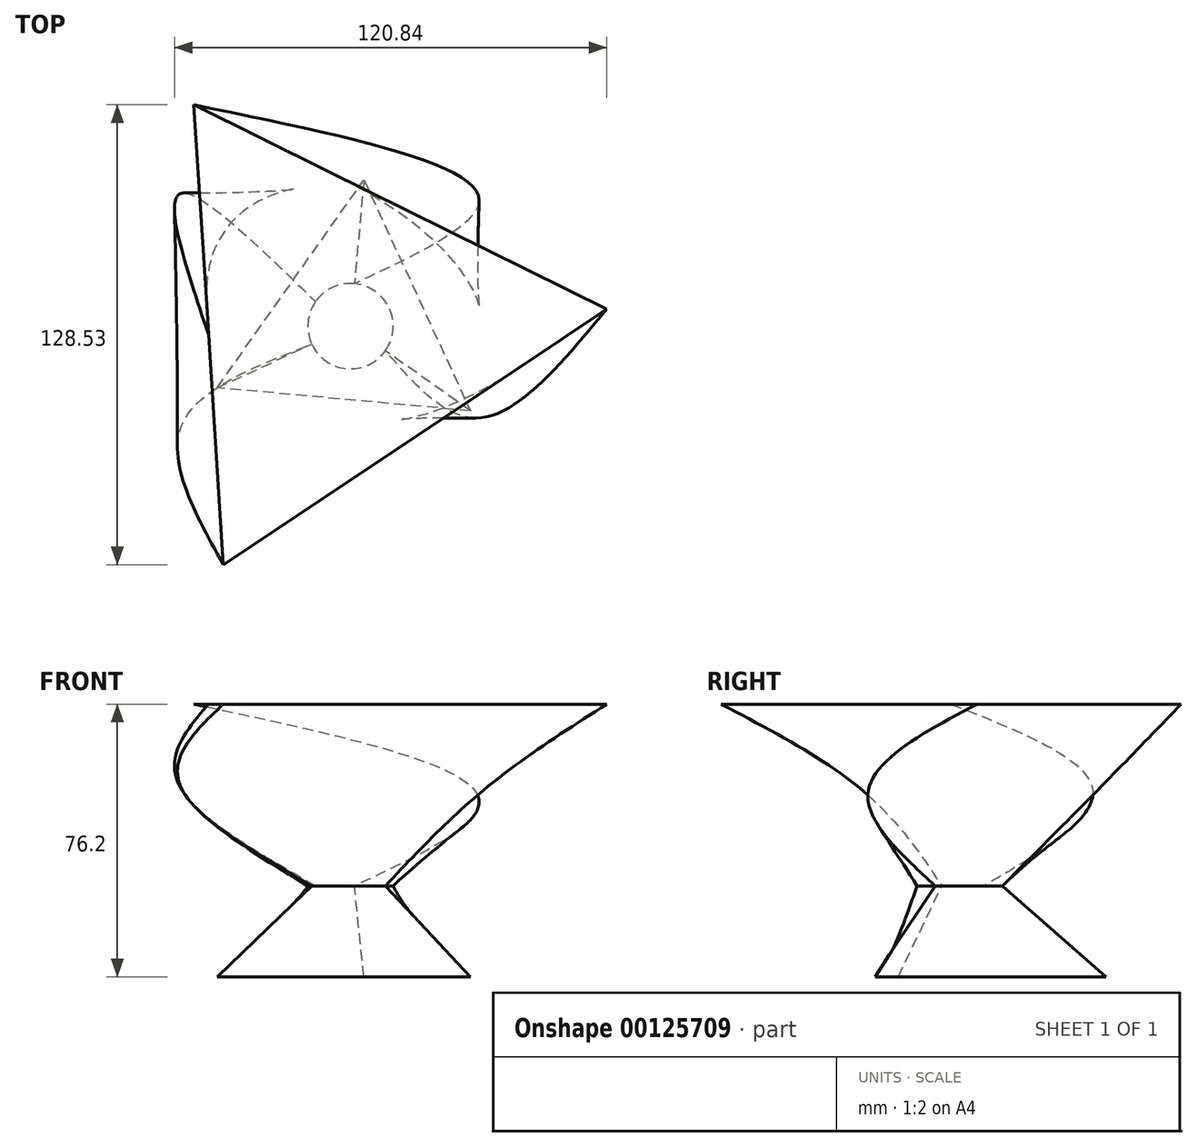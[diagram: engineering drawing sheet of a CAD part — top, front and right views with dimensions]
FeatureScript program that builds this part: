
annotation { "Feature Type Name" : "Feature", "Feature Type Description" : "" }
export const myFeature = defineFeature(function(context is Context, id is Id, definition is map)
    precondition{}
    {
        {
            var Q0;
            Q0=qCreatedBy(makeId("Top.planeOp"),FACE);
            cPlane(context, id + "F0", {"entities" : qUnion([Q0]), "cplaneType" : CPlaneType.OFFSET, "offset" : 25.4 * mm, "width" : 152.4 * mm, "height" : 152.4 * mm});
        }
        {
            var Q0;
            Q0=qCreatedBy(id+"F0.planeOp",FACE);
            cPlane(context, id + "F1", {"entities" : qUnion([Q0]), "cplaneType" : CPlaneType.OFFSET, "offset" : 25.4 * mm, "width" : 152.4 * mm, "height" : 152.4 * mm});
        }
        {
            var Q0;
            Q0=qCreatedBy(id+"F1.planeOp",FACE);
            cPlane(context, id + "F2", {"entities" : qUnion([Q0]), "cplaneType" : CPlaneType.OFFSET, "offset" : 25.4 * mm, "width" : 152.4 * mm, "height" : 152.4 * mm});
        }
        {
            var Q0;
            Q0=qCreatedBy(id+"F0.planeOp",FACE);
            var sketch = newSketch(context, id + "F3", { "sketchPlane" : qUnion([Q0])});
            skCircle(sketch, "E0", {"center": v(0, 0) * mm, "radius": 11.93 * mm});
            skSolve(sketch);
        }
        {
            var Q0;
            Q0=qCreatedBy(makeId("Top.planeOp"),FACE);
            var sketch = newSketch(context, id + "F4", { "sketchPlane" : qUnion([Q0])});
            skCircle(sketch, "E1.cCircle", {"center": v(0, 0) * mm, "radius": 20.52 * mm, "construction": true});
            skLineSegment(sketch, "E1.0", {"start": v(3.74, 40.88) * mm, "end": v(33.53, -23.68) * mm});
            skLineSegment(sketch, "E1.1", {"start": v(33.53, -23.68) * mm, "end": v(-37.27, -17.2) * mm});
            skLineSegment(sketch, "E1.2", {"start": v(-37.27, -17.2) * mm, "end": v(3.74, 40.88) * mm});
            skPoint(sketch, "E1.0.midPoint", {"position": v(18.64, 8.6) * mm});
            skSolve(sketch);
        }
        {
            var Q0;
            Q0=makeQuery(id+"F4.imprint","IMPRINT",FACE,{"disambiguationData":[TD([[makeQuery(id+"F4.imprint","IMPRINT",EDGE,{"derivedFrom":sQuery(id+"F4.wireOp",EDGE,"E1.0")}),-1.0]])]});
            var Q1;
            Q1=makeQuery(id+"F3.imprint","IMPRINT",FACE,{"disambiguationData":[TD([[makeQuery(id+"F3.imprint","IMPRINT",EDGE,{"derivedFrom":sQuery(id+"F3.wireOp",EDGE,"E0")}),1.0]])]});
            loft(context, id + "F5", {"sheetProfilesArray" : [{ "sheetProfileEntities" : qUnion([Q0]) }, { "sheetProfileEntities" : qUnion([Q1]) }]});
        }
        {
            var Q0;
            Q0=qCreatedBy(id+"F1.planeOp",FACE);
            var sketch = newSketch(context, id + "F6", { "sketchPlane" : qUnion([Q0])});
            skLineSegment(sketch, "E2.bottom", {"start": v(35.54, -25.67) * mm, "end": v(-46.17, -25.67) * mm});
            skLineSegment(sketch, "E2.top", {"start": v(35.54, 37.2) * mm, "end": v(-46.17, 37.2) * mm});
            skLineSegment(sketch, "E2.left", {"start": v(35.54, -25.67) * mm, "end": v(35.54, 37.2) * mm});
            skLineSegment(sketch, "E2.right", {"start": v(-46.17, -25.67) * mm, "end": v(-46.17, 37.2) * mm});
            skSolve(sketch);
        }
        {
            var Q0;
            Q0=qCreatedBy(id+"F2.planeOp",FACE);
            var sketch = newSketch(context, id + "F7", { "sketchPlane" : qUnion([Q0])});
            skCircle(sketch, "E3.cCircle", {"center": v(-2.58, 0) * mm, "radius": 37.18 * mm, "construction": true});
            skLineSegment(sketch, "E3.0", {"start": v(71.63, 4.79) * mm, "end": v(-35.54, -66.66) * mm});
            skLineSegment(sketch, "E3.1", {"start": v(-35.54, -66.66) * mm, "end": v(-43.83, 61.87) * mm});
            skLineSegment(sketch, "E3.2", {"start": v(-43.83, 61.87) * mm, "end": v(71.63, 4.79) * mm});
            skPoint(sketch, "E3.0.midPoint", {"position": v(18.05, -30.94) * mm});
            skSolve(sketch);
        }
        {
            var Q1;
            Q1=makeQuery(id+"F7.imprint","IMPRINT",FACE,{"disambiguationData":[TD([[makeQuery(id+"F7.imprint","IMPRINT",EDGE,{"derivedFrom":sQuery(id+"F7.wireOp",EDGE,"E3.0")}),-1.0]])]});
            var Q2;
            Q2=makeQuery(id+"F6.imprint","IMPRINT",FACE,{"disambiguationData":[TD([[makeQuery(id+"F6.imprint","IMPRINT",EDGE,{"derivedFrom":sQuery(id+"F6.wireOp",EDGE,"E2.bottom")}),-1.0]])]});
            var Q3;
            Q3=makeQuery(id+"F5.opLoft","CAP_FACE",FACE,{"disambiguationData":[OSD([makeQuery(id+"F3.imprint","IMPRINT",FACE,{"disambiguationData":[TD([[makeQuery(id+"F3.imprint","IMPRINT",EDGE,{"derivedFrom":sQuery(id+"F3.wireOp",EDGE,"E0")}),1.0]])]})])],"isStart":true});
            loft(context, id + "F8", {"operationType" : NewBodyOperationType.ADD, "sheetProfilesArray" : [{ "sheetProfileEntities" : qUnion([Q1]) }, { "sheetProfileEntities" : qUnion([Q2]) }, { "sheetProfileEntities" : qUnion([Q3]) }]});
        }
    });
